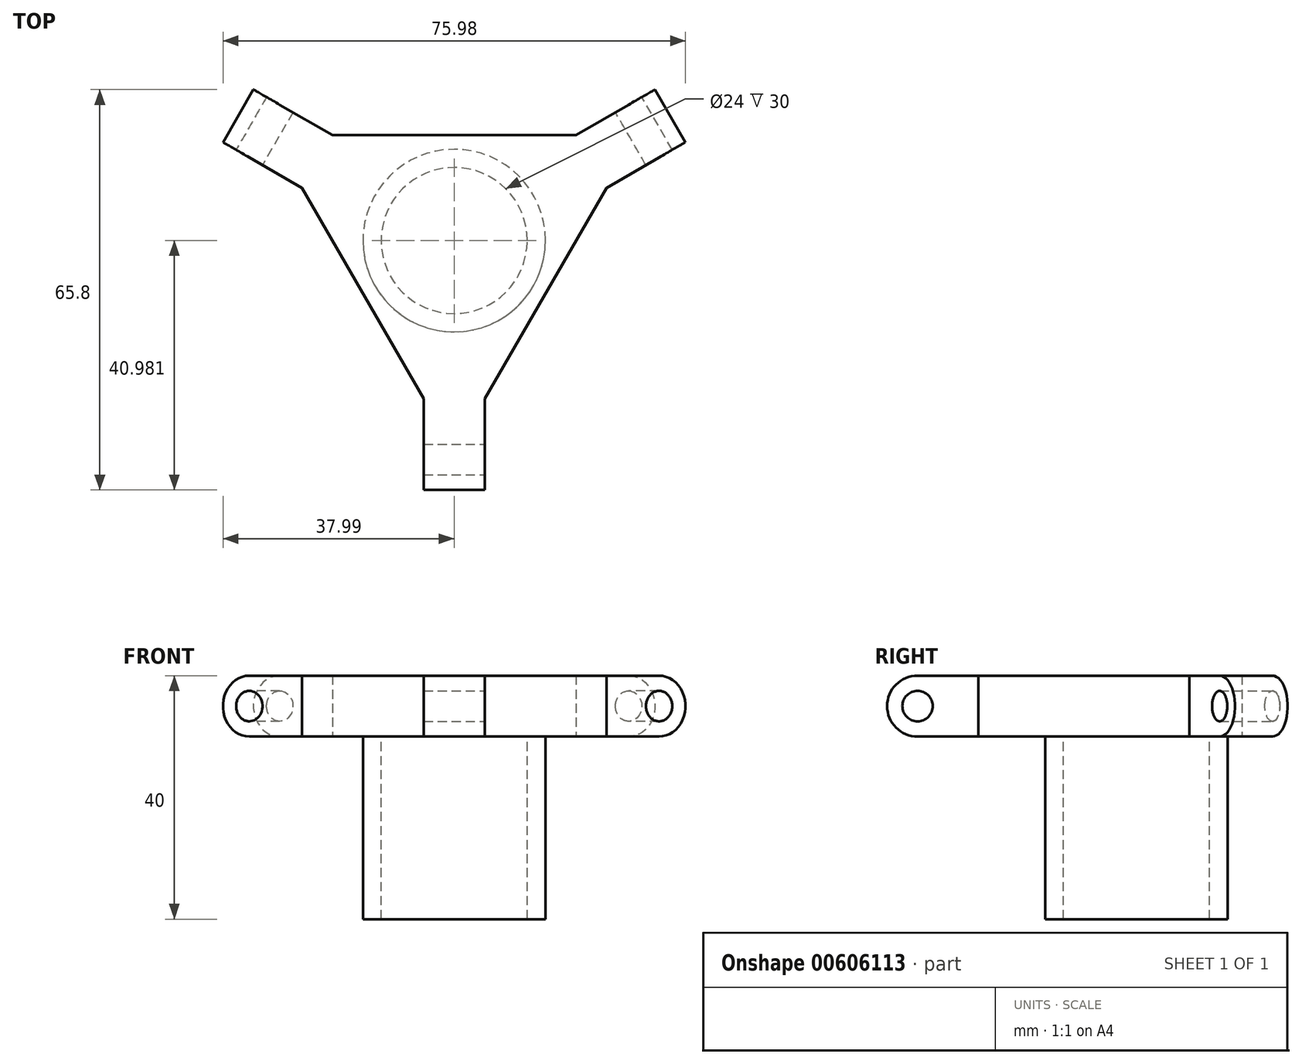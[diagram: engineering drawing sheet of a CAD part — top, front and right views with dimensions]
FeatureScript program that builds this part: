
annotation { "Feature Type Name" : "Feature", "Feature Type Description" : "" }
export const myFeature = defineFeature(function(context is Context, id is Id, definition is map)
    precondition{}
    {
        {
            var Q0;
            Q0=qCreatedBy(makeId("Top.planeOp"),FACE);
            var sketch = newSketch(context, id + "F0", { "sketchPlane" : qUnion([Q0])});
            skLineSegment(sketch, "E0", {"start": v(-30, 51.96) * mm, "end": v(30, 51.96) * mm});
            skLineSegment(sketch, "E1", {"start": v(30, 51.96) * mm, "end": v(0, 0) * mm});
            skLineSegment(sketch, "E2", {"start": v(0, 0) * mm, "end": v(-30, 51.96) * mm});
            skLineSegment(sketch, "E3", {"start": v(-20, 51.96) * mm, "end": v(-25, 43.3) * mm});
            skLineSegment(sketch, "E4", {"start": v(-5, 8.66) * mm, "end": v(5, 8.66) * mm});
            skLineSegment(sketch, "E5", {"start": v(20, 51.96) * mm, "end": v(25, 43.3) * mm});
            skLineSegment(sketch, "E6", {"start": v(-25, 43.3) * mm, "end": v(-33.66, 48.3) * mm});
            skLineSegment(sketch, "E7", {"start": v(-33.66, 48.3) * mm, "end": v(-28.66, 56.96) * mm});
            skLineSegment(sketch, "E8.top", {"start": v(-5, -1.34) * mm, "end": v(5, -1.34) * mm});
            skLineSegment(sketch, "E8.left", {"start": v(-5, 8.66) * mm, "end": v(-5, -1.34) * mm});
            skLineSegment(sketch, "E8.right", {"start": v(5, 8.66) * mm, "end": v(5, -1.34) * mm});
            skLineSegment(sketch, "E9", {"start": v(20, 51.96) * mm, "end": v(28.66, 56.96) * mm});
            skLineSegment(sketch, "E10", {"start": v(28.66, 56.96) * mm, "end": v(33.66, 48.3) * mm});
            skLineSegment(sketch, "E11", {"start": v(33.66, 48.3) * mm, "end": v(25, 43.3) * mm});
            skLineSegment(sketch, "E12", {"start": v(-28.66, 56.96) * mm, "end": v(-20, 51.96) * mm});
            skSolve(sketch);
        }
        {
            var Q0;
            Q0 = qSketchRegion(id + "F0", true);
            extrude(context, id + "F1", {"entities" : qUnion([Q0]), "endBound" : BoundingType.SYMMETRIC, "depth" : 10 * mm, "offsetDistance" : 25.4 * mm});
        }
        {
            var Q0;
            Q0=makeQuery(id+"F1.opExtrude","SWEPT_FACE",FACE,{"disambiguationData":[OSD([sQuery(id+"F0.wireOp",EDGE,"E6")])]});
            var sketch = newSketch(context, id + "F2", { "sketchPlane" : qUnion([Q0])});
            skCircle(sketch, "E13", {"center": v(-53.3, 0) * mm, "radius": 5 * mm});
            skSolve(sketch);
        }
        {
            var Q0;
            {var subQ1=sQuery(id+"F0.wireOp",EDGE,"E6");var subQ2=makeQuery(id+"F1.opExtrude","SWEPT_EDGE",EDGE,{"disambiguationData":[OSD([subQ1,sQuery(id+"F0.wireOp",EDGE,"E7")])]});Q0=makeQuery(id+"F2.imprint","IMPRINT",FACE,{"disambiguationData":[TD([[makeQuery(id+"F2.imprint","IMPRINT",EDGE,{"derivedFrom":subQ2}),-1.0]])]});}
            extrude(context, id + "F3", {"entities" : qUnion([Q0]), "operationType" : NewBodyOperationType.ADD, "oppositeDirection" : true, "depth" : 10 * mm, "offsetDistance" : 25.4 * mm});
        }
        {
            var Q0;
            Q0=makeQuery(id+"F1.opExtrude","SWEPT_FACE",FACE,{"disambiguationData":[OSD([sQuery(id+"F0.wireOp",EDGE,"E9")])]});
            var sketch = newSketch(context, id + "F4", { "sketchPlane" : qUnion([Q0])});
            skCircle(sketch, "E14", {"center": v(-53.3, 0) * mm, "radius": 5 * mm});
            skSolve(sketch);
        }
        {
            var Q0;
            {var subQ1=sQuery(id+"F0.wireOp",EDGE,"E9");var subQ2=makeQuery(id+"F1.opExtrude","SWEPT_EDGE",EDGE,{"disambiguationData":[OSD([subQ1,sQuery(id+"F0.wireOp",EDGE,"E10")])]});Q0=makeQuery(id+"F4.imprint","IMPRINT",FACE,{"disambiguationData":[TD([[makeQuery(id+"F4.imprint","IMPRINT",EDGE,{"derivedFrom":subQ2}),-1.0]])]});}
            extrude(context, id + "F5", {"entities" : qUnion([Q0]), "operationType" : NewBodyOperationType.ADD, "oppositeDirection" : true, "depth" : 10 * mm, "offsetDistance" : 25.4 * mm});
        }
        {
            var Q0;
            Q0=makeQuery(id+"F1.opExtrude","SWEPT_FACE",FACE,{"disambiguationData":[OSD([sQuery(id+"F0.wireOp",EDGE,"E8.right")])]});
            var sketch = newSketch(context, id + "F6", { "sketchPlane" : qUnion([Q0])});
            skCircle(sketch, "E15", {"center": v(-1.34, 0) * mm, "radius": 5 * mm});
            skSolve(sketch);
        }
        {
            var Q0;
            {var subQ1=sQuery(id+"F0.wireOp",EDGE,"E8.right");var subQ2=makeQuery(id+"F1.opExtrude","SWEPT_EDGE",EDGE,{"disambiguationData":[OSD([sQuery(id+"F0.wireOp",EDGE,"E8.top"),subQ1])]});Q0=makeQuery(id+"F6.imprint","IMPRINT",FACE,{"disambiguationData":[TD([[makeQuery(id+"F6.imprint","IMPRINT",EDGE,{"derivedFrom":subQ2}),-1.0]])]});}
            extrude(context, id + "F7", {"entities" : qUnion([Q0]), "operationType" : NewBodyOperationType.ADD, "oppositeDirection" : true, "depth" : 10 * mm, "offsetDistance" : 25.4 * mm});
        }
        {
            var Q0;
            {var subQ0=sQuery(id+"F0.wireOp",EDGE,"E8.right");Q0=makeQuery(id+"F7.boolean.opBoolean","MERGE",FACE,{"derivedFrom":[makeQuery(id+"F1.opExtrude","SWEPT_FACE",FACE,{"disambiguationData":[OSD([subQ0])]}),makeQuery(id+"F7.opExtrude","CAP_FACE",FACE,{"disambiguationData":[OSD([sQuery(id+"F0.wireOp",EDGE,"E8.top"),subQ0,sQuery(id+"F6.wireOp",EDGE,"E15")])],"isStart":true})]});}
            var sketch = newSketch(context, id + "F8", { "sketchPlane" : qUnion([Q0])});
            skCircle(sketch, "E16", {"center": v(-1.34, 0) * mm, "radius": 2.5 * mm});
            skSolve(sketch);
        }
        {
            var Q0;
            Q0 = qSketchRegion(id + "F8", true);
            extrude(context, id + "F9", {"entities" : qUnion([Q0]), "operationType" : NewBodyOperationType.REMOVE, "oppositeDirection" : true, "depth" : 25.4 * mm, "offsetDistance" : 25.4 * mm});
        }
        {
            var Q0;
            {var subQ0=sQuery(id+"F0.wireOp",EDGE,"E9");Q0=makeQuery(id+"F5.boolean.opBoolean","MERGE",FACE,{"derivedFrom":[makeQuery(id+"F1.opExtrude","SWEPT_FACE",FACE,{"disambiguationData":[OSD([subQ0])]}),makeQuery(id+"F5.opExtrude","CAP_FACE",FACE,{"disambiguationData":[OSD([subQ0,sQuery(id+"F0.wireOp",EDGE,"E10"),sQuery(id+"F4.wireOp",EDGE,"E14")])],"isStart":true})]});}
            var sketch = newSketch(context, id + "F10", { "sketchPlane" : qUnion([Q0])});
            skCircle(sketch, "E17", {"center": v(-53.3, 0) * mm, "radius": 2.5 * mm});
            skSolve(sketch);
        }
        {
            var Q0;
            Q0 = qSketchRegion(id + "F10", true);
            extrude(context, id + "F11", {"entities" : qUnion([Q0]), "operationType" : NewBodyOperationType.REMOVE, "oppositeDirection" : true, "depth" : 25.4 * mm, "offsetDistance" : 25.4 * mm});
        }
        {
            var Q0;
            {var subQ0=sQuery(id+"F0.wireOp",EDGE,"E6");Q0=makeQuery(id+"F3.boolean.opBoolean","MERGE",FACE,{"derivedFrom":[makeQuery(id+"F1.opExtrude","SWEPT_FACE",FACE,{"disambiguationData":[OSD([subQ0])]}),makeQuery(id+"F3.opExtrude","CAP_FACE",FACE,{"disambiguationData":[OSD([subQ0,sQuery(id+"F0.wireOp",EDGE,"E7"),sQuery(id+"F2.wireOp",EDGE,"E13")])],"isStart":true})]});}
            var sketch = newSketch(context, id + "F12", { "sketchPlane" : qUnion([Q0])});
            skCircle(sketch, "E18", {"center": v(-53.3, 0) * mm, "radius": 2.5 * mm});
            skSolve(sketch);
        }
        {
            var Q0;
            Q0 = qSketchRegion(id + "F12", true);
            extrude(context, id + "F13", {"entities" : qUnion([Q0]), "operationType" : NewBodyOperationType.REMOVE, "oppositeDirection" : true, "depth" : 25.4 * mm, "offsetDistance" : 25.4 * mm});
        }
        {
            var Q0;
            Q0=makeQuery(id+"F1.opExtrude","CAP_FACE",FACE,{"disambiguationData":[OSD([sQuery(id+"F0.wireOp",EDGE,"E0"),sQuery(id+"F0.wireOp",EDGE,"E1"),sQuery(id+"F0.wireOp",EDGE,"E2"),sQuery(id+"F0.wireOp",EDGE,"E6"),sQuery(id+"F0.wireOp",EDGE,"E7"),sQuery(id+"F0.wireOp",EDGE,"E8.top"),sQuery(id+"F0.wireOp",EDGE,"E8.left"),sQuery(id+"F0.wireOp",EDGE,"E8.right"),sQuery(id+"F0.wireOp",EDGE,"E9"),sQuery(id+"F0.wireOp",EDGE,"E10"),sQuery(id+"F0.wireOp",EDGE,"E11"),sQuery(id+"F0.wireOp",EDGE,"E12")])],"isStart":true});
            var sketch = newSketch(context, id + "F14", { "sketchPlane" : qUnion([Q0])});
            skLineSegment(sketch, "E19", {"start": v(0, -51.96) * mm, "end": v(0, 0) * mm});
            skLineSegment(sketch, "E20", {"start": v(31.16, -52.63) * mm, "end": v(-15, -25.98) * mm});
            skLineSegment(sketch, "E21", {"start": v(-31.16, -52.63) * mm, "end": v(15, -25.98) * mm});
            skCircle(sketch, "E22", {"center": v(0, -34.64) * mm, "radius": 15 * mm});
            skCircle(sketch, "E23", {"center": v(0, -34.64) * mm, "radius": 12 * mm});
            skSolve(sketch);
        }
        {
            var Q0;
            Q0 = qSketchRegion(id + "F14", true);
            extrude(context, id + "F15", {"entities" : qUnion([Q0]), "operationType" : NewBodyOperationType.ADD, "depth" : 30 * mm, "offsetDistance" : 25.4 * mm});
        }
    });
